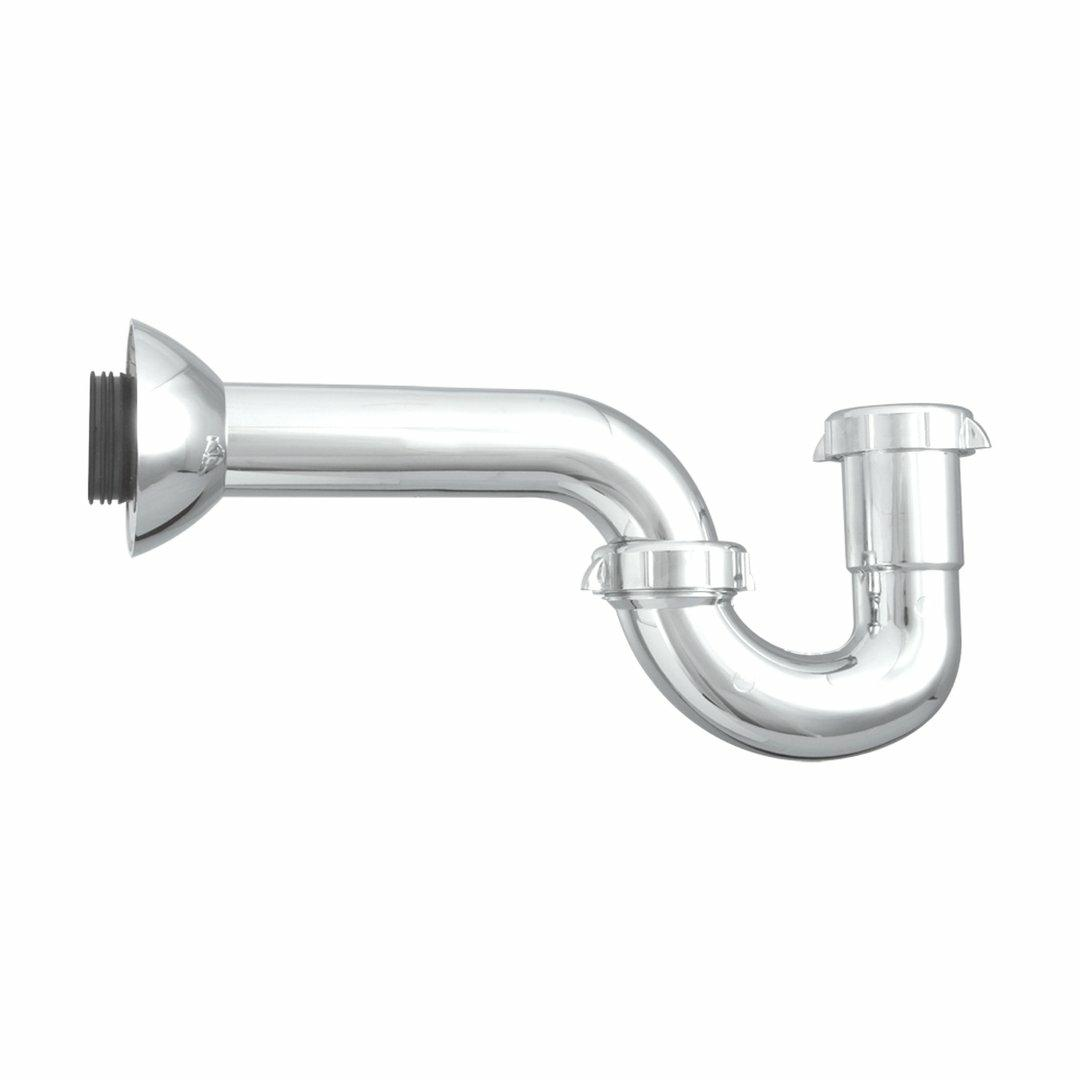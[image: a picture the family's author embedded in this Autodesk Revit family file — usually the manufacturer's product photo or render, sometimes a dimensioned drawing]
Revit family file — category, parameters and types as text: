
# Revit family: BIM_M1-3003-11
name_source: partatom
category: Aparatos sanitarios
units: mm (PartAtom-declared; Revit-internal decimal feet)

## family parameters
Activar corte en vistas = No
Anfitrión = Cara
Compartido = No
Corte con vacíos al cargar = No
Cota de conector redondo = Usar diámetro
Mantener orientación de anotación = No
Número OmniClass = 23.31.11.00
Punto de cálculo de habitación = No
Tipo de pieza = Normal

## types (1)
- M1-3003-11
    Acabado = Cepillado Brillante
    Alto = 160 mm  [stored 0.524934 ft]
    Ancho = 940 mm  [stored 3.08399 ft]
    Conexión AC = Sí
    Conexión AF = Sí
    Conexión de residuos = No
    Conexión de ventilación = No
    Date Modified = 08-08-2025
    Descripción = Lavaplatos en acero
    Elevación por defecto = 0 mm  [stored 0 ft]
    Fabricante = Gricol
    Garantia Especifica = 5 años
    Imagen de tipo = FOTO LAVAPLATOS EN ACERO POCETA DERECHA 94 x 48 cm.JPG
    Largo = 480 mm  [stored 1.5748 ft]
    Link Ficha Tecnica = https://infotecnica.gricol.com
    Material = Acero inoxidable
    Materiales del producto = Acero Inoxidable
    Modelo = M1-3003-11
    Nota clave = Perforación para instalar grifería monomando
    Peso = 3.80 kg
    Product Name = Lavaplatos Poceta Derecha 94 X 48 Cm Con Complementos
    Resistencia a Corrosión = Si
    Sitio web = https://www.gricol.com
    Tipo de Uso = Residencial
    URL = https://www.gricol.com

note: [stored X ft] marks values corroborated as IEEE doubles in the binary element streams (Revit-internal decimal feet)

## geometry (parser evidence)
native form markers: Blend x4, Sweep x13
no freeform markers — native parametric forms only
